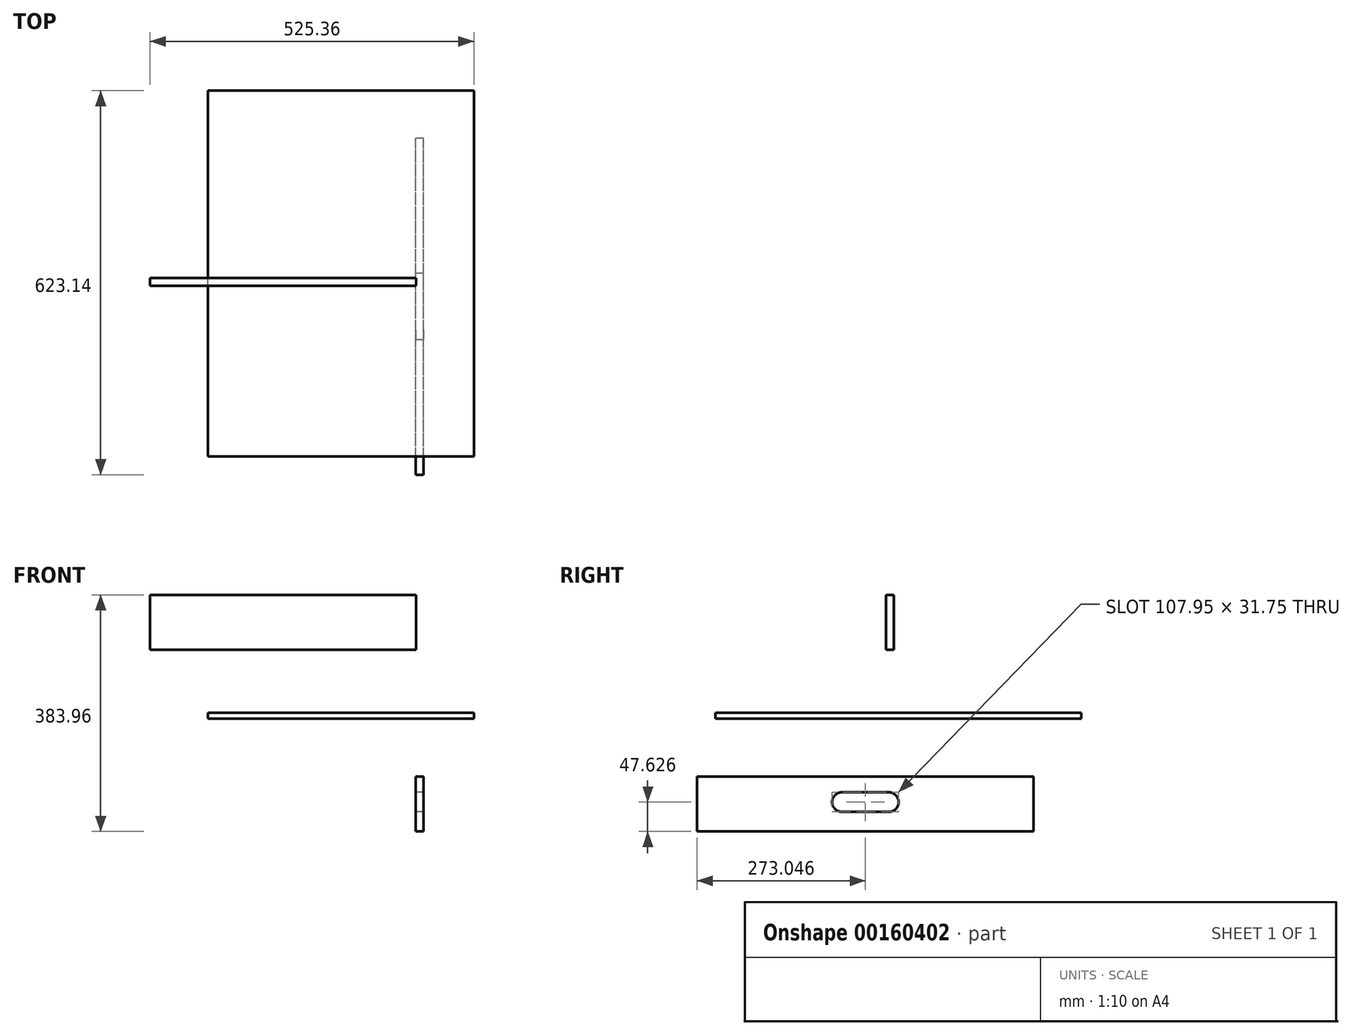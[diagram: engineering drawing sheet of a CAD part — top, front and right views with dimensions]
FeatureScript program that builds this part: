
annotation { "Feature Type Name" : "Feature", "Feature Type Description" : "" }
export const myFeature = defineFeature(function(context is Context, id is Id, definition is map)
    precondition{}
    {
        {
            var Q0;
            Q0=qCreatedBy(makeId("Top.planeOp"),FACE);
            var sketch = newSketch(context, id + "F0", { "sketchPlane" : qUnion([Q0])});
            skLineSegment(sketch, "E0.bottom", {"start": v(-337.55, -289.83) * mm, "end": v(94.25, -289.83) * mm});
            skLineSegment(sketch, "E0.top", {"start": v(-337.55, 303.9) * mm, "end": v(94.25, 303.9) * mm});
            skLineSegment(sketch, "E0.left", {"start": v(-337.55, -289.83) * mm, "end": v(-337.55, 303.9) * mm});
            skLineSegment(sketch, "E0.right", {"start": v(94.25, -289.83) * mm, "end": v(94.25, 303.9) * mm});
            skLineSegment(sketch, "E1.0", {"start": v(-337.55, 289.6) * mm, "end": v(94.25, 289.6) * mm});
            skLineSegment(sketch, "E2.0", {"start": v(-337.55, -275.54) * mm, "end": v(94.25, -275.54) * mm});
            skSolve(sketch);
        }
        {
            var Q0;
            Q0 = qSketchRegion(id + "F0", true);
            extrude(context, id + "F1", {"entities" : qUnion([Q0]), "depth" : 9.52 * mm});
        }
        {
            var Q0;
            Q0=qCreatedBy(makeId("Front.planeOp"),FACE);
            var sketch = newSketch(context, id + "F2", { "sketchPlane" : qUnion([Q0])});
            skLineSegment(sketch, "E3.bottom", {"start": v(-431.1, 200.74) * mm, "end": v(0.7, 200.74) * mm});
            skLineSegment(sketch, "E3.top", {"start": v(-431.1, 111.84) * mm, "end": v(0.7, 111.84) * mm});
            skLineSegment(sketch, "E3.left", {"start": v(-431.1, 200.74) * mm, "end": v(-431.1, 111.84) * mm});
            skLineSegment(sketch, "E3.right", {"start": v(0.7, 200.74) * mm, "end": v(0.7, 111.84) * mm});
            skSolve(sketch);
        }
        {
            var Q0;
            Q0=makeQuery(id+"F2.imprint","IMPRINT",FACE,{"disambiguationData":[TD([[makeQuery(id+"F2.imprint","IMPRINT",EDGE,{"derivedFrom":sQuery(id+"F2.wireOp",EDGE,"E3.bottom")}),-1.0]])]});
            extrude(context, id + "F3", {"entities" : qUnion([Q0]), "depth" : 12.7 * mm});
        }
        {
            var Q0;
            Q0=qCreatedBy(makeId("Right.planeOp"),FACE);
            var sketch = newSketch(context, id + "F4", { "sketchPlane" : qUnion([Q0])});
            skLineSegment(sketch, "E4.bottom", {"start": v(-319.24, -94.32) * mm, "end": v(226.86, -94.32) * mm});
            skLineSegment(sketch, "E4.top", {"start": v(-319.24, -183.22) * mm, "end": v(226.86, -183.22) * mm});
            skLineSegment(sketch, "E4.left", {"start": v(-319.24, -94.32) * mm, "end": v(-319.24, -183.22) * mm});
            skArc(sketch, "E5", {"start": v(-84.3, -119.72) * mm, "mid": v(-100.17, -135.6) * mm, "end": v(-84.3, -151.47) * mm});
            skArc(sketch, "E6", {"start": v(-8.1, -151.47) * mm, "mid": v(7.78, -135.6) * mm, "end": v(-8.1, -119.72) * mm});
            skLineSegment(sketch, "E7", {"start": v(-84.3, -151.47) * mm, "end": v(-8.1, -151.47) * mm});
            skLineSegment(sketch, "E8", {"start": v(-8.1, -119.72) * mm, "end": v(-84.3, -119.72) * mm});
            skLineSegment(sketch, "E9", {"start": v(226.86, -94.32) * mm, "end": v(226.86, -183.22) * mm});
            skSolve(sketch);
        }
        {
            var Q0;
            Q0=makeQuery(id+"F4.imprint","IMPRINT",FACE,{"disambiguationData":[TD([[makeQuery(id+"F4.imprint","IMPRINT",EDGE,{"derivedFrom":sQuery(id+"F4.wireOp",EDGE,"E4.bottom")}),-1.0]])]});
            extrude(context, id + "F5", {"entities" : qUnion([Q0]), "depth" : 12.7 * mm});
        }
    });
